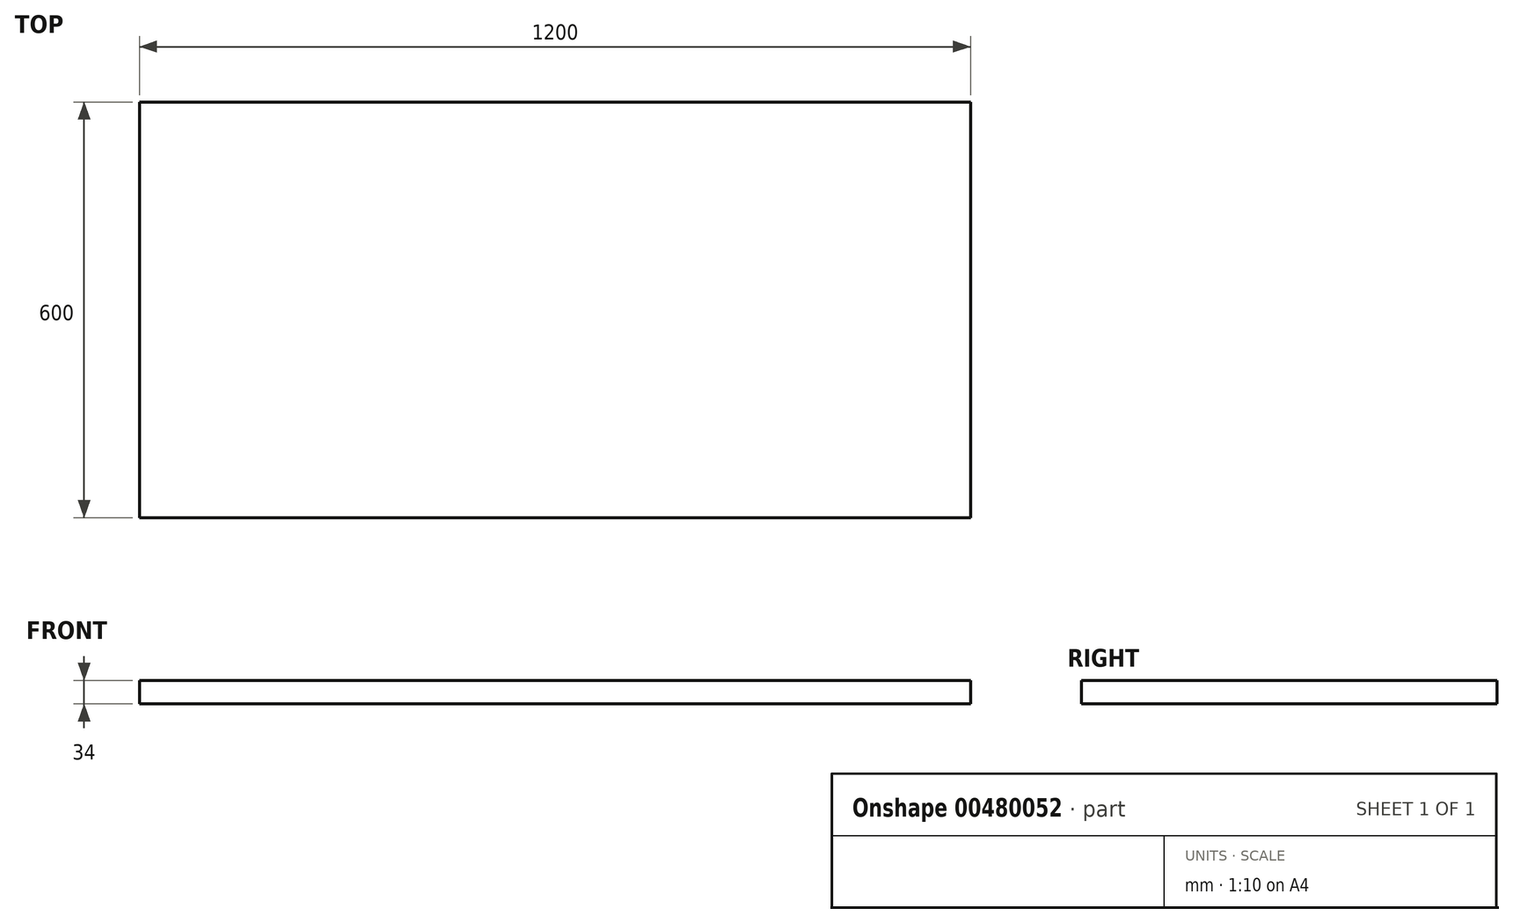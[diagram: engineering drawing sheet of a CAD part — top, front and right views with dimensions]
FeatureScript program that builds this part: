
annotation { "Feature Type Name" : "Feature", "Feature Type Description" : "" }
export const myFeature = defineFeature(function(context is Context, id is Id, definition is map)
    precondition{}
    {
        {
            var Q0;
            Q0=qCreatedBy(makeId("Top.planeOp"),FACE);
            var sketch = newSketch(context, id + "F0", { "sketchPlane" : qUnion([Q0])});
            skLineSegment(sketch, "E0.bottom", {"start": v(600, 300) * mm, "end": v(-600, 300) * mm});
            skLineSegment(sketch, "E0.top", {"start": v(600, -300) * mm, "end": v(-600, -300) * mm});
            skLineSegment(sketch, "E0.left", {"start": v(600, 300) * mm, "end": v(600, -300) * mm});
            skLineSegment(sketch, "E0.right", {"start": v(-600, 300) * mm, "end": v(-600, -300) * mm});
            skPoint(sketch, "E0.middle", {"position": v(0, 0) * mm});
            skSolve(sketch);
        }
        {
            var Q0;
            Q0=makeQuery(id+"F0.imprint","IMPRINT",FACE,{"disambiguationData":[TD([[makeQuery(id+"F0.imprint","IMPRINT",EDGE,{"derivedFrom":sQuery(id+"F0.wireOp",EDGE,"E0.bottom")}),1.0]])]});
            extrude(context, id + "F1", {"entities" : qUnion([Q0]), "depth" : 34 * mm});
        }
    });
